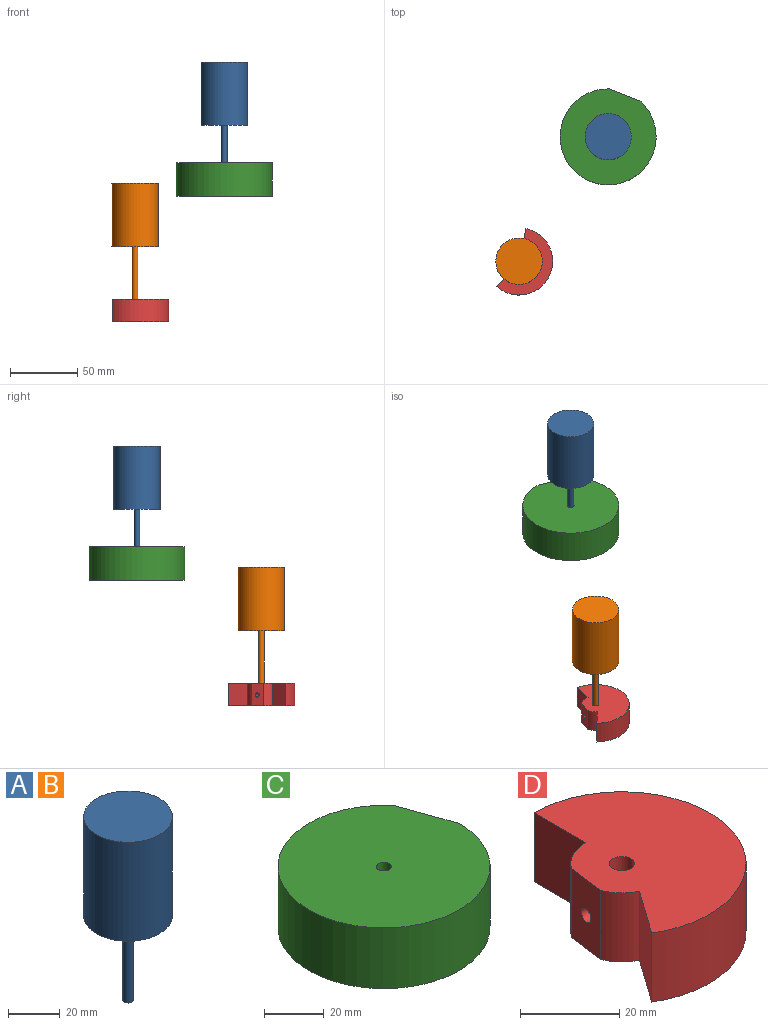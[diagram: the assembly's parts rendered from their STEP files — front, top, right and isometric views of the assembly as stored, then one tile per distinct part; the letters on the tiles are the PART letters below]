
ASSEMBLY  parts=4 mates=2
PART A: 5 faces, bbox 34.5x34.5x87 mm
  f0: cylinder r=2.12mm len=40mm, axis (0,0,-1), area 532.4mm2, adj f1,f4
  f1: plane 4.24x4.24mm, normal (0,0,-1), area 14.1mm2, adj f0
  f2: cylinder r=17.23mm len=47mm, axis (0,0,-1), area 5087.7mm2, adj f3,f4
  f3: plane 34.46x34.46mm, normal (0,0,1), area 932.5mm2, adj f2
  f4: plane 34.46x34.46mm, normal (0,0,-1), area 918.4mm2, adj f0,f2
PART B: same geometry as A
PART C: 5 faces, bbox 71.3x71.3x25 mm
  f0: plane 25x22.71mm, normal (0.94,0.34,0), area 602.8mm2, adj f2,f3,f4
  f1: cylinder r=2.5mm len=25mm, axis (0,0,-1), area 392.7mm2, adj f3,f4
  f2: cylinder r=35.67mm len=71.33mm, axis (0,0,-1), area 4987.7mm2, adj f0,f3,f4
  f3: plane 71.33x71.33mm, normal (0,0,1), area 3942.9mm2, adj f0,f1,f2
  f4: plane 71.33x71.33mm, normal (0,0,-1), area 3942.9mm2, adj f0,f1,f2
PART D: 10 faces, bbox 37.9x50x17 mm
  f0: cylinder r=2.5mm len=17mm, axis (0,0,-1), area 258.7mm2, adj f7,f8,f9
  f1: plane 17x9.6mm, normal (-0.99,0.13,0), area 156.6mm2, adj f2,f6,f7,f8,f9
  f2: cylinder r=10.28mm len=17mm, axis (0,0,-1), area 135.8mm2, adj f1,f3,f7,f8
  f3: plane 17x12.08mm, normal (-0.82,0.58,0), area 252mm2, adj f2,f4,f7,f8
  f4: cylinder r=25mm len=50mm, axis (0,0,-1), area 1565.5mm2, adj f3,f5,f7,f8
  f5: plane 17x14.72mm, normal (-1,0,0), area 250.2mm2, adj f4,f6,f7,f8
  f6: cylinder r=10.28mm len=17mm, axis (0,0,-1), area 166.5mm2, adj f1,f5,f7,f8
  f7: plane 50x37.89mm, normal (0,0,1), area 1252.7mm2, adj f0,f1,f2,f3,f4,f5,f6
  f8: plane 50x37.89mm, normal (0,0,-1), area 1252.7mm2, adj f0,f1,f2,f3,f4,f5,f6
  f9: cylinder r=1.58mm len=7.49mm, axis (-0.99,0.13,0), area 68.1mm2, adj f0,f1
PLACE A t=(64.31,88.03,51.63)mm fixed
PLACE B t=(-1.95,-4.38,-38.46)mm fixed
PLACE C rot(axis=(0,0,1),48.6deg) t=(117.34,106.47,55.89)mm
PLACE D rot(axis=(0,0,-1),11.9deg) t=(-1.95,-4.38,-37.46)mm
MATE cylindrical B.f0 <-> D.f0  axis (0,0,-1) through (-1.95,-4.38,-21.46)mm
MATE cylindrical A.f0 <-> C.f1  axis (0,0,-1) through (64.31,88.03,88.63)mm
